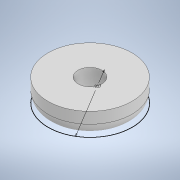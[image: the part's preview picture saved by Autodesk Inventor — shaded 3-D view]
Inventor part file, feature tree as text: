
AUTODESK INVENTOR PART (.ipt)
format: ipt  version: 2020 (Build 240168000, 168)  size: 126,976 bytes
history: native  units: in
note: dims shown in document units (in); Inventor stores cm internally (conversion verified against a paired STEP export)
features: sketch x1, extrude x1, hole x1, fillet x1
ambient origin geometry x8: Origin, YZ Plane, XZ Plane, XY Plane, X Axis, Y Axis, Z Axis, Center Point
bodies: Solid1 (feature_tree)
feature tree (4):
  sketch  "Sketch1"  dims[d0=0.937in d1=0.25in d2=0.0in d3=0.266in d4=0.75in d5=0.438in d6=0.0625in d7=0.5635in d8=1.0in d9=0.8108in d10=0.125in]
  extrude  "Extrusion1"  Depth=0.25in TaperAngle=0.0deg
  hole  "Hole1"  [1 undecoded]
  fillet  "Fillet1"  [1 undecoded]
note: 2 required parameter values undecoded (feature->parameter linkage not recoverable at this tier; creation-order binding heuristic only, values carry confidence <= 0.55)
